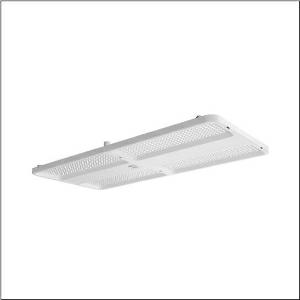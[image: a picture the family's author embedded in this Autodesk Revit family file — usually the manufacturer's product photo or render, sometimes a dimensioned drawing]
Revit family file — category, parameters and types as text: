
# Revit family: highbay_11_maxi_51hn12db4lda01
name_source: partatom
category: Lighting Fixtures
units: mm (PartAtom-declared; Revit-internal decimal feet)

## family parameters
Cut with Voids When Loaded = No
Host = Face
Light Source = No
Part Type = Normal
Room Calculation Point = No
Round Connector Dimension = Use Diameter
Shared = No

## types (1)
- --- (1 x LED, 26000 lm, 125.9 W, 4000K)
    Apparent Load = 126 VA
    CIE Flux Codes = 87 98 100 100 100
    Color Rendering = 80
    Color Temperature = 4000K
    Default Elevation = 1800 mm
    Description = high bay luminaire Highbay 11 maxi; direct symmetric wide distribution, light control with lens of PMMA; UGR ≤ 19 (X = 4H | Y = 8H | S = 0.25H | reflection values 70/50/20); luminous flux: 26.000lm; light colour: 840, colour temperature: 4000K, MacAdam ≤ 2 SDCM (initial), colour rendering: CRI > 80; luminous efficacy: 206,5lm/W; rated service life: 100.000h (L95/B50) at AT= 25°C; control: Bluetooth® Mesh; for wireless networking: Node multi-sensor luminaire for setting up a local control solution without a higher-level application controller, intelligence completely integrated into the luminaire; with auto-swarm function: leading lighting creates safety. The function is already active without any „out-of-the-box“ commissioning; commissioning is not necessary thanks to „out-of-the-box“ functions: basic functions (presence lighting, follow-up times, fading times, etc.) are already preset at the factory; no control line such as DALI between the Node multi-sensor luminaires and Nodes is required, wireless integration of other Node luminaires and Node multi-sensor luminaires into the network is possible; number of Node multi-sensor luminaires in the project can be expanded as required, network sizes > 300 Nodes can be realized; can also be connected to lighting or building automation via various gateways upon request; integrated DALI2 ECG provides luminaire data (according to IEC62386, Part 251), energy data (Part 252), and monitoring and analytics data (Part 253) to higher-level systems for further processing; luminaire with PIR sensor (passive-infrared); with light sensor; luminaire connection: terminal, 5-pole, max. 2.5mm² (cable entry for one cable, Ø 8.5..16mm); mains connection: 230..240V, AC 50/60Hz; connected load: 125,9W; protection rating (complete): IP65; insulation class (complete): insulation class I (protective earthing); protection symbol: D; certification: CE, ENEC, VDE, UKCA; internal wiring halogen-free; luminaire corresponds to IFS (International Featured Standards) requirements for safety and quality in the food industry; LABS conformity tested according to VDMA 24364:2018-05; housing frame of high-performance plastic PA6, matt traffic white (RAL 9016); cover of PMMA; dimension (LxWxH): 946 x 442 x 72mm; permissible operating ambient temperature: -20..+45°C (reducing of maximum allowable ambient temperature of 5°C with ceiling mounting); packaging unit: 1 piece; (delivery without accessories; please order mounting accessories separately)
    Height = 72 mm  [stored 0.23622 ft]
    Lamp = 1 x LED
    Lamp Light Flux = 26000 lm
    Lamp Power = 125.9 W
    Lamp count = 1
    Length = 946 mm
    Luminous efficacy = 207 lm/W
    Manufacturer = Siteco
    ModVariant = No
    Model = 51HN12DB4LDA01
    Mounting Place = Ceiling
    Mounting Type = Pendant
    Number of Poles = 1
    OnlyDefault = Yes
    Power Factor = 1
    Product Name = Highbay 11 maxi
    Product group = high bay luminaire
    ProductGroupID = 901
    Protection Class = Protection class I
    Protection Degree = IP 65
    RLX_Detail_Level = 1
    RLX_Emergency_Light_Flux = 0 lm
    RLX_Emergency_Type = 0
    RLX_Emergency_Type_DB = No
    RlxData = <blob elided: 127877 chars, md5=1ad28421>
    Socket = socket
    Standby Power = 0 W
    System Light Flux = 26000 lm
    System Power = 126 W
    Type Comments = factory setting: luminous flux: 100 % | dim-lin: 254 | 584 mA
    Type Image = l_1363267.jpg
    URL = http://relux.com
    VarID = @adj_025195
    Voltage = 0 V
    Weight = 0.00 kg
    Width = 442 mm

note: [stored X ft] marks values corroborated as IEEE doubles in the binary element streams (Revit-internal decimal feet)

## geometry (parser evidence)
native form markers: Blend x4, Sweep x10
no freeform markers — native parametric forms only
